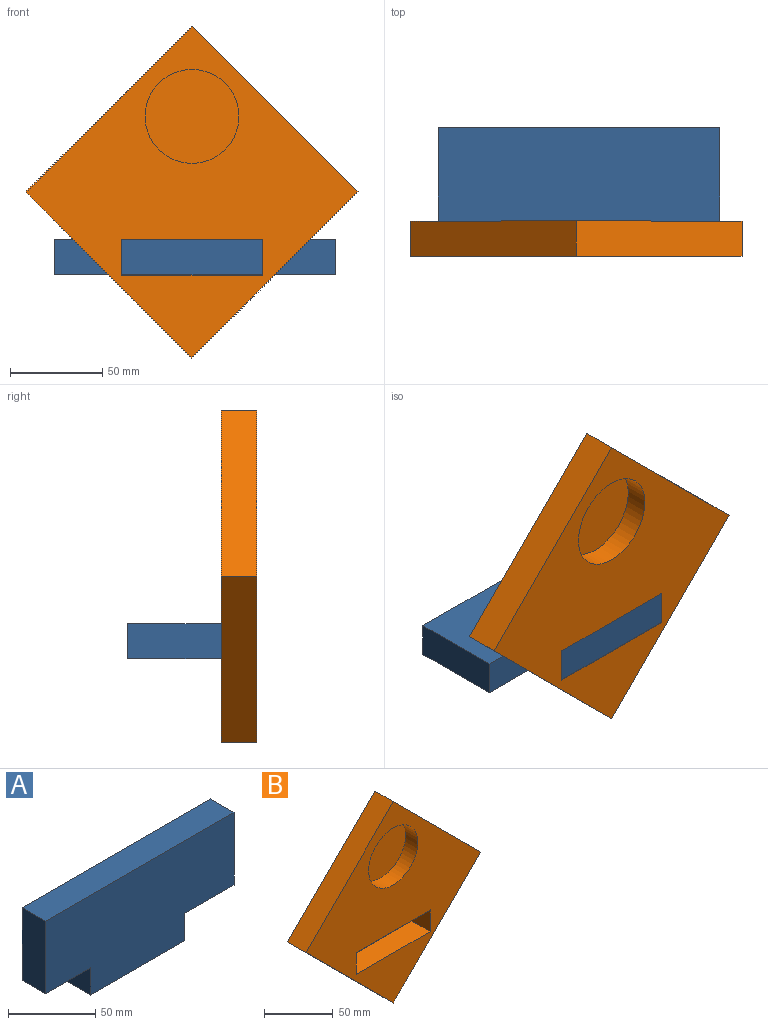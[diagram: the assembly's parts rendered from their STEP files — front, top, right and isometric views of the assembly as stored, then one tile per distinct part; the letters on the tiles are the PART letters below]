
ASSEMBLY  parts=2 mates=1
PART A: 10 faces, bbox 152.4x19.1x69.9 mm
  f0: plane 152.4x19.05mm, normal (0,0,1), area 2903.2mm2, adj f1,f7,f8,f9
  f1: plane 50.8x19.05mm, normal (-1,0,0), area 967.7mm2, adj f0,f2,f8,f9
  f2: plane 36.43x19.05mm, normal (0,0,-1), area 693.9mm2, adj f1,f3,f8,f9
  f3: plane 19.05x19.05mm, normal (-1,0,0), area 362.9mm2, adj f2,f4,f8,f9
  f4: plane 76.2x19.05mm, normal (0,0,-1), area 1451.6mm2, adj f3,f5,f8,f9
  f5: plane 19.05x19.05mm, normal (1,0,0), area 362.9mm2, adj f4,f6,f8,f9
  f6: plane 39.77x19.05mm, normal (0,0,-1), area 757.7mm2, adj f5,f7,f8,f9
  f7: plane 50.8x19.05mm, normal (1,0,0), area 967.7mm2, adj f0,f6,f8,f9
  f8: plane 152.4x69.85mm, normal (0,-1,0), area 9193.5mm2, adj f0,f1,f2,f3,f4,f5,f6,f7
  f9: plane 152.4x69.85mm, normal (0,1,0), area 9193.5mm2, adj f0,f1,f2,f3,f4,f5,f6,f7
PART B: 12 faces, bbox 179.6x19.1x179.6 mm
  f0: plane 89.8x89.8mm, normal (0.71,0,0.71), area 2419.3mm2, adj f1,f7,f8,f9
  f1: plane 89.8x89.8mm, normal (-0.71,0,0.71), area 2419.3mm2, adj f0,f2,f8,f9
  f2: plane 89.8x89.8mm, normal (-0.71,0,-0.71), area 2419.3mm2, adj f1,f7,f8,f9
  f3: plane 76.2x19.05mm, normal (0,0,1), area 1451.6mm2, adj f4,f6,f8,f9
  f4: plane 19.3x19.05mm, normal (1,0,0), area 367.7mm2, adj f3,f5,f8,f9
  f5: plane 76.2x19.05mm, normal (0,0,-1), area 1451.6mm2, adj f4,f6,f8,f9
  f6: plane 19.3x19.05mm, normal (-1,0,0), area 367.7mm2, adj f3,f5,f8,f9
  f7: plane 89.8x89.8mm, normal (0.71,0,-0.71), area 2419.3mm2, adj f0,f2,f8,f9
  f8: plane 179.61x179.61mm, normal (0,-1,0), area 12631.2mm2, adj f0,f1,f2,f3,f4,f5,f6,f7
  f9: plane 179.61x179.61mm, normal (0,1,0), area 14658mm2, adj f0,f1,f2,f3,f4,f5,f6,f7
  f10: cylinder r=25.4mm len=50.8mm, axis (0,-1,0), area 2026.8mm2, adj f8,f11
  f11: plane 50.8x50.8mm, normal (0,-1,0), area 2026.8mm2, adj f10
PLACE A rot(axis=(-1,0,0),90deg) t=(-5.19,48.19,-24.83)mm
PLACE B t=(18.62,38.67,20.05)mm
MATE fastened A.f2 <-> B.f9  axis (0,-1,0) through (-19.48,48.19,-5.78)mm
